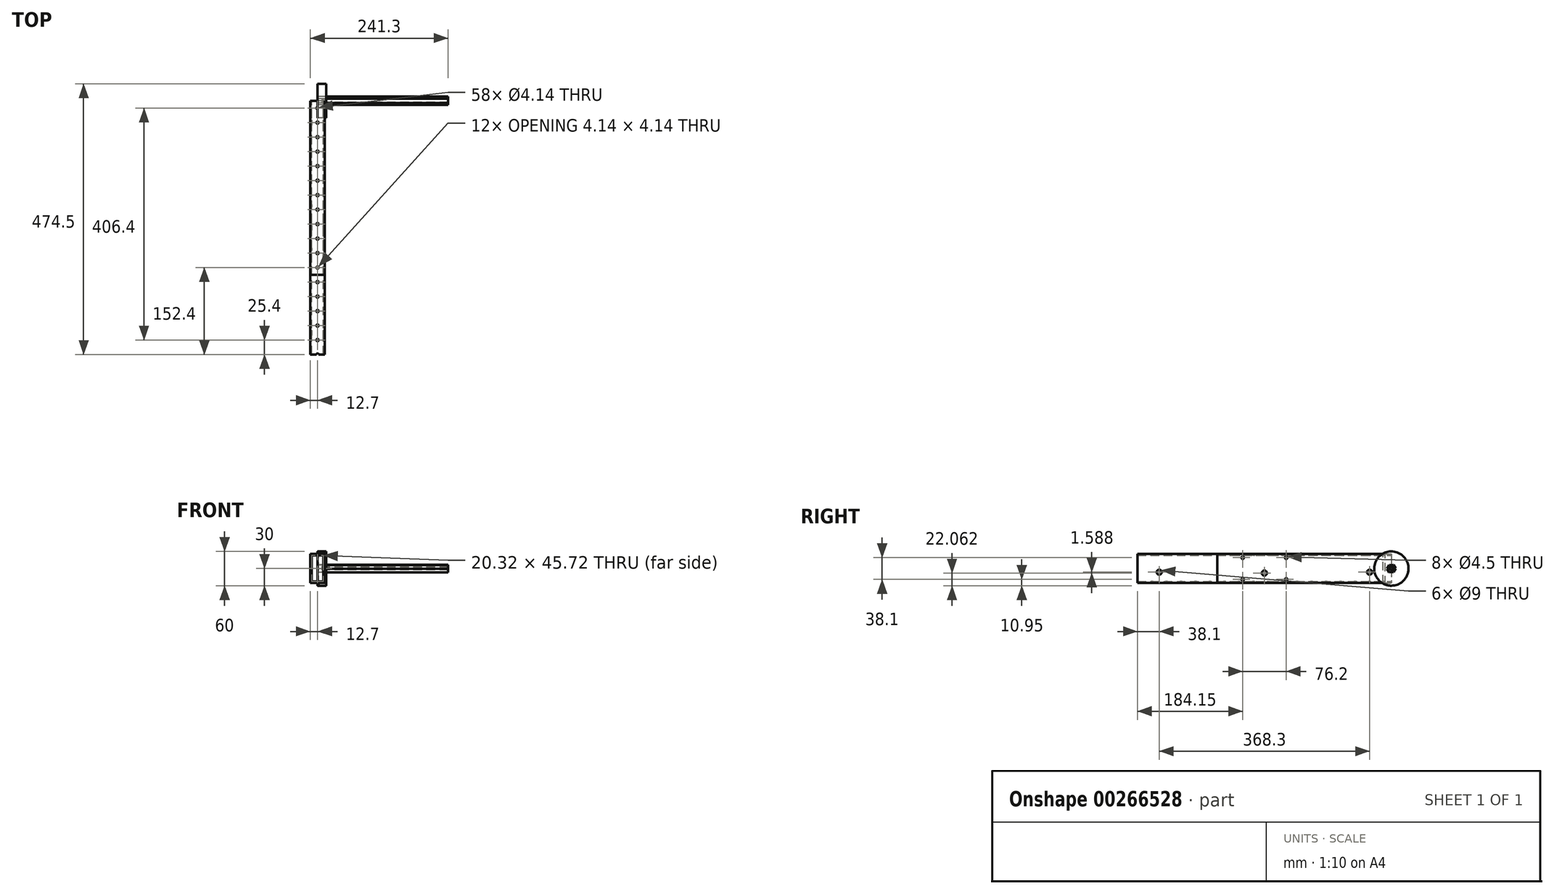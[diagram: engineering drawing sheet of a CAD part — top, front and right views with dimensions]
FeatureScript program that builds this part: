
annotation { "Feature Type Name" : "Feature", "Feature Type Description" : "" }
export const myFeature = defineFeature(function(context is Context, id is Id, definition is map)
    precondition{}
    {
        {
            var Q0;
            Q0=qCreatedBy(makeId("Front.planeOp"),FACE);
            var sketch = newSketch(context, id + "F0", { "sketchPlane" : qUnion([Q0])});
            skLineSegment(sketch, "E0.bottom", {"start": v(12.7, 25.4) * mm, "end": v(-12.7, 25.4) * mm});
            skLineSegment(sketch, "E0.top", {"start": v(12.7, -25.4) * mm, "end": v(-12.7, -25.4) * mm});
            skLineSegment(sketch, "E0.left", {"start": v(12.7, 25.4) * mm, "end": v(12.7, -25.4) * mm});
            skLineSegment(sketch, "E0.right", {"start": v(-12.7, 25.4) * mm, "end": v(-12.7, -25.4) * mm});
            skPoint(sketch, "E0.middle", {"position": v(0, 0) * mm});
            skLineSegment(sketch, "E1.0", {"start": v(10.16, 22.86) * mm, "end": v(-10.16, 22.86) * mm});
            skLineSegment(sketch, "E1.1", {"start": v(10.16, 22.86) * mm, "end": v(10.16, -22.86) * mm});
            skLineSegment(sketch, "E1.2", {"start": v(10.16, -22.86) * mm, "end": v(-10.16, -22.86) * mm});
            skLineSegment(sketch, "E1.3", {"start": v(-10.16, 22.86) * mm, "end": v(-10.16, -22.86) * mm});
            skSolve(sketch);
        }
        {
            var Q0;
            Q0=makeQuery(id+"F0.imprint","IMPRINT",FACE,{"disambiguationData":[TD([[makeQuery(id+"F0.imprint","IMPRINT",EDGE,{"derivedFrom":sQuery(id+"F0.wireOp",EDGE,"E0.bottom")}),1.0]])]});
            extrude(context, id + "F1", {"entities" : qUnion([Q0]), "depth" : 444.5 * mm});
        }
        {
            var Q0;
            Q0=makeQuery(id+"F1.opExtrude","SWEPT_FACE",FACE,{"disambiguationData":[OSD([sQuery(id+"F0.wireOp",EDGE,"E0.bottom")])]});
            var sketch = newSketch(context, id + "F2", { "sketchPlane" : qUnion([Q0])});
            skPoint(sketch, "E2", {"position": v(0, -12.7) * mm});
            skCircle(sketch, "E3", {"center": v(0, -12.7) * mm, "radius": 2.07 * mm});
            skCircle(sketch, "E4.0.1.0", {"center": v(0, -38.1) * mm, "radius": 2.07 * mm});
            skCircle(sketch, "E4.0.2.0", {"center": v(0, -63.5) * mm, "radius": 2.07 * mm});
            skCircle(sketch, "E4.0.3.0", {"center": v(0, -88.9) * mm, "radius": 2.07 * mm});
            skCircle(sketch, "E4.0.4.0", {"center": v(0, -114.3) * mm, "radius": 2.07 * mm});
            skCircle(sketch, "E4.0.5.0", {"center": v(0, -139.7) * mm, "radius": 2.07 * mm});
            skCircle(sketch, "E4.0.6.0", {"center": v(0, -165.1) * mm, "radius": 2.07 * mm});
            skCircle(sketch, "E4.0.7.0", {"center": v(0, -190.5) * mm, "radius": 2.07 * mm});
            skCircle(sketch, "E4.0.8.0", {"center": v(0, -215.9) * mm, "radius": 2.07 * mm});
            skCircle(sketch, "E4.0.9.0", {"center": v(0, -241.3) * mm, "radius": 2.07 * mm});
            skCircle(sketch, "E4.0.10.0", {"center": v(0, -266.7) * mm, "radius": 2.07 * mm});
            skCircle(sketch, "E4.0.11.0", {"center": v(0, -292.1) * mm, "radius": 2.07 * mm});
            skCircle(sketch, "E4.0.12.0", {"center": v(0, -317.5) * mm, "radius": 2.07 * mm});
            skCircle(sketch, "E4.0.13.0", {"center": v(0, -342.9) * mm, "radius": 2.07 * mm});
            skCircle(sketch, "E4.0.14.0", {"center": v(0, -368.3) * mm, "radius": 2.07 * mm});
            skCircle(sketch, "E4.0.15.0", {"center": v(0, -393.7) * mm, "radius": 2.07 * mm});
            skCircle(sketch, "E4.0.16.0", {"center": v(0, -419.1) * mm, "radius": 2.07 * mm});
            skLineSegment(sketch, "E4.direction1", {"start": v(0, -12.7) * mm, "end": v(25.4, -12.45) * mm, "construction": true});
            skLineSegment(sketch, "E4.direction2", {"start": v(0, -12.7) * mm, "end": v(0, -38.1) * mm, "construction": true});
            skCircle(sketch, "E5.0.0.17", {"center": v(0, -444.5) * mm, "radius": 2.07 * mm});
            skSolve(sketch);
        }
        {
            var Q0;
            Q0=makeQuery(id+"F1.opExtrude","SWEPT_FACE",FACE,{"disambiguationData":[OSD([sQuery(id+"F0.wireOp",EDGE,"E0.left")])]});
            var sketch = newSketch(context, id + "F3", { "sketchPlane" : qUnion([Q0])});
            skPoint(sketch, "E6", {"position": v(-406.4, -6.35) * mm});
            skCircle(sketch, "E7", {"center": v(-406.4, -6.35) * mm, "radius": 30 * mm, "construction": true});
            skPoint(sketch, "E8", {"position": v(-222.25, -7.94) * mm});
            skLineSegment(sketch, "E9", {"start": v(-222.25, 25.4) * mm, "end": v(-222.25, -25.4) * mm, "construction": true});
            skPoint(sketch, "E10.MirrorP", {"position": v(-38.1, -6.35) * mm});
            skCircle(sketch, "E11", {"center": v(-222.25, -7.94) * mm, "radius": 30 * mm, "construction": true});
            skCircle(sketch, "E12", {"center": v(-38.1, -6.35) * mm, "radius": 30 * mm, "construction": true});
            skLineSegment(sketch, "E13.bottom", {"start": v(-184.15, 19.05) * mm, "end": v(-260.35, 19.05) * mm, "construction": true});
            skLineSegment(sketch, "E13.top", {"start": v(-184.15, -19.05) * mm, "end": v(-260.35, -19.05) * mm, "construction": true});
            skLineSegment(sketch, "E13.left", {"start": v(-184.15, 19.05) * mm, "end": v(-184.15, -19.05) * mm, "construction": true});
            skLineSegment(sketch, "E13.right", {"start": v(-260.35, 19.05) * mm, "end": v(-260.35, -19.05) * mm, "construction": true});
            skPoint(sketch, "E13.middle", {"position": v(-222.25, 0) * mm});
            skSolve(sketch);
        }
        {
            var Q0;
            Q0=sQuery(id+"F3.wireOp",VERTEX,"E6");
            var Q1;
            Q1=sQuery(id+"F3.wireOp",VERTEX,"E8");
            var Q2;
            Q2=sQuery(id+"F3.wireOp",VERTEX,"E10.MirrorP");
            var Q3;
            Q3=makeQuery(id+"F1.opExtrude","SWEPT_BODY",BODY,{"disambiguationData":[OSD([sQuery(id+"F0.wireOp",EDGE,"E0.bottom"),sQuery(id+"F0.wireOp",EDGE,"E0.top"),sQuery(id+"F0.wireOp",EDGE,"E0.left"),sQuery(id+"F0.wireOp",EDGE,"E0.right"),sQuery(id+"F0.wireOp",EDGE,"E1.0"),sQuery(id+"F0.wireOp",EDGE,"E1.1"),sQuery(id+"F0.wireOp",EDGE,"E1.2"),sQuery(id+"F0.wireOp",EDGE,"E1.3")])]});
            hole(context, id + "F4", {"style" : HoleStyle.SIMPLE, "endStyle" : HoleEndStyle.THROUGH, "holeDiameter" : 9 * mm, "isTappedThrough" : true, "tappedDepth" : 7.14 * mm, "tapClearance" : 3, "locations" : qUnion([Q0, Q1, Q2]), "scope" : qUnion([Q3])});
        }
        {
            var Q0;
            Q0=qCreatedBy(makeId("Right.planeOp"),FACE);
            var sketch = newSketch(context, id + "F5", { "sketchPlane" : qUnion([Q0])});
            skCircle(sketch, "E14", {"center": v(0, 0) * mm, "radius": 30 * mm});
            skSolve(sketch);
        }
        {
            var Q0;
            Q0=makeQuery(id+"F5.imprint","IMPRINT",FACE,{"disambiguationData":[TD([[makeQuery(id+"F5.imprint","IMPRINT",EDGE,{"derivedFrom":sQuery(id+"F5.wireOp",EDGE,"E14")}),1.0]])]});
            extrude(context, id + "F6", {"entities" : qUnion([Q0]), "depth" : 15 * mm});
        }
        {
            var Q0;
            Q0=makeQuery(id+"F0.imprint","IMPRINT",FACE,{"disambiguationData":[TD([[makeQuery(id+"F0.imprint","IMPRINT",EDGE,{"derivedFrom":sQuery(id+"F0.wireOp",EDGE,"E0.bottom")}),1.0]])]});
            extrude(context, id + "F7", {"entities" : qUnion([Q0]), "depth" : 304.8 * mm});
        }
        {
            var Q0;
            Q0 = qSketchRegion(id + "F2", true);
            extrude(context, id + "F8", {"entities" : qUnion([Q0]), "operationType" : NewBodyOperationType.REMOVE, "endBound" : BoundingType.THROUGH_ALL, "oppositeDirection" : true, "depth" : 25.4 * mm});
        }
        {
            var Q0;
            Q0=qCreatedBy(makeId("Right.planeOp"),FACE);
            var sketch = newSketch(context, id + "F9", { "sketchPlane" : qUnion([Q0])});
            skCircle(sketch, "E15.cCircle", {"center": v(0, 0) * mm, "radius": 6.35 * mm, "construction": true});
            skLineSegment(sketch, "E15.0", {"start": v(7.33, 0.15) * mm, "end": v(3.8, -6.27) * mm});
            skLineSegment(sketch, "E15.1", {"start": v(3.8, -6.27) * mm, "end": v(-3.54, -6.42) * mm});
            skLineSegment(sketch, "E15.2", {"start": v(-3.54, -6.42) * mm, "end": v(-7.33, -0.15) * mm});
            skLineSegment(sketch, "E15.3", {"start": v(-7.33, -0.15) * mm, "end": v(-3.8, 6.27) * mm});
            skLineSegment(sketch, "E15.4", {"start": v(-3.8, 6.27) * mm, "end": v(3.54, 6.42) * mm});
            skLineSegment(sketch, "E15.5", {"start": v(3.54, 6.42) * mm, "end": v(7.33, 0.15) * mm});
            skPoint(sketch, "E15.0.midPoint", {"position": v(5.56, -3.06) * mm});
            skSolve(sketch);
        }
        {
            var Q0;
            Q0 = qSketchRegion(id + "F9", true);
            extrude(context, id + "F10", {"entities" : qUnion([Q0]), "depth" : 228.6 * mm});
        }
        {
            var Q0;
            Q0=sQuery(id+"F9.wireOp",VERTEX,"E15.cCircle.center");
            var Q1;
            Q1=makeQuery(id+"F10.opExtrude","SWEPT_BODY",BODY,{"disambiguationData":[OSD([sQuery(id+"F9.wireOp",EDGE,"E15.0"),sQuery(id+"F9.wireOp",EDGE,"E15.1"),sQuery(id+"F9.wireOp",EDGE,"E15.2"),sQuery(id+"F9.wireOp",EDGE,"E15.3"),sQuery(id+"F9.wireOp",EDGE,"E15.4"),sQuery(id+"F9.wireOp",EDGE,"E15.5")])]});
            hole(context, id + "F11", {"style" : HoleStyle.SIMPLE, "endStyle" : HoleEndStyle.THROUGH, "oppositeDirection" : true, "standardTappedOrClearance" : lookupTablePath({ "standard" : "ANSI", "fit" : "Normal (ASME)", "size" : "#10", "type" : "Clearance" }), "standardBlindInLast" : lookupTablePath({ "fit" : "Free", "standard" : "ANSI", "size" : "#10", "type" : "Clearance" }), "holeDiameter" : 5.1 * mm, "isTappedThrough" : true, "tappedDepth" : 7.14 * mm, "tapClearance" : 3, "locations" : qUnion([Q0]), "scope" : qUnion([Q1])});
        }
        {
            var Q0;
            Q0=sQuery(id+"F3.wireOp",VERTEX,"E13.right.start");
            var Q1;
            Q1=sQuery(id+"F3.wireOp",VERTEX,"E13.left.start");
            var Q2;
            Q2=sQuery(id+"F3.wireOp",VERTEX,"E13.left.end");
            var Q3;
            Q3=sQuery(id+"F3.wireOp",VERTEX,"E13.right.end");
            var Q4;
            Q4=makeQuery(id+"F1.opExtrude","SWEPT_BODY",BODY,{"disambiguationData":[OSD([sQuery(id+"F0.wireOp",EDGE,"E0.bottom"),sQuery(id+"F0.wireOp",EDGE,"E0.top"),sQuery(id+"F0.wireOp",EDGE,"E0.left"),sQuery(id+"F0.wireOp",EDGE,"E0.right"),sQuery(id+"F0.wireOp",EDGE,"E1.0"),sQuery(id+"F0.wireOp",EDGE,"E1.1"),sQuery(id+"F0.wireOp",EDGE,"E1.2"),sQuery(id+"F0.wireOp",EDGE,"E1.3")])]});
            hole(context, id + "F12", {"style" : HoleStyle.SIMPLE, "endStyle" : HoleEndStyle.THROUGH, "standardTappedOrClearance" : lookupTablePath({ "standard" : "ANSI", "fit" : "Normal (ASME)", "size" : "#8", "type" : "Clearance" }), "standardBlindInLast" : lookupTablePath({ "fit" : "Free", "standard" : "ANSI", "size" : "#8", "type" : "Clearance" }), "holeDiameter" : 4.5 * mm, "isTappedThrough" : true, "tappedDepth" : 7.14 * mm, "tapClearance" : 3, "locations" : qUnion([Q0, Q1, Q2, Q3]), "scope" : qUnion([Q4])});
        }
    });
